# Revit family: ELP2_63_UN_Lightline_ETK
name_source: partatom
category: Lighting Fixtures
units: mm (PartAtom-declared; Revit-internal decimal feet)

## family parameters
Always vertical = No
Cut with Voids When Loaded = No
Light Source = Yes
OmniClass Number = 23.80.70.00
OmniClass Title = Lighting
Part Type = Normal
Room Calculation Point = Yes
Round Connector Dimension = Use Diameter
Shared = No
Work Plane-Based = No

## types (128) — shared parameters
Assembly Code = 63.0
Color Filter = 16777215
Description = Lightline
Dimming Lamp Color Temperature Shift = <None>
Emit Shape Visible in Rendering = No
Emit from Rectangle Length = 68 mm
Emit from Rectangle Width = 1482 mm  [stored 4.8622 ft]
IfcExportAs = IfcLightFixtureType
IfcExportType = USERDEFINED
Lamp = LED
Length = 1482 mm  [stored 4.8622 ft]
Luminaire_Body_Material = PPS Plastic
Manufacturer = ETK licht B.V.
Model = ELP2
Tilt Angle = 90.00°
URL = https://www.etk.nl
Voltage = 230 V

## per-type parameters (varying)
| type | Apparent Load | Photometric Web File | Wattage Comments |
| ELP.8673.15 | 118 VA | ELP.8673.15.ies | 118 W |
| ELP.8670.15 | 118 VA | ELP.8670.15.ies | 118 W |
| ELP.8663.15 | 118 VA | ELP.8663.15.ies | 118 W |
| ELP.8660.15 | 118 VA | ELP.8660.15.ies | 118 W |
| ELP.8653.15 | 80 VA | ELP.8653.15.ies | 80 W |
| ELP.8650.15 | 80 VA | ELP.8650.15.ies | 80 W |
| ELP.8643.15 | 80 VA | ELP.8643.15.ies | 80 W |
| ELP.8640.15 | 80 VA | ELP.8640.15.ies | 80 W |
| ELP.8633.15 | 61 VA | ELP.8633.15.ies | 61 W |
| ELP.8630.15 | 61 VA | ELP.8630.15.ies | 61 W |
| ELP.8623.15 | 61 VA | ELP.8623.15.ies | 61 W |
| ELP.8620.15 | 61 VA | ELP.8620.15.ies | 61 W |
| ELP.8613.15 | 43 VA | ELP.8613.15.ies | 43 W |
| ELP.8610.15 | 43 VA | ELP.8610.15.ies | 43 W |
| ELP.8603.15 | 43 VA | ELP.8603.15.ies | 43 W |
| ELP.8600.15 | 43 VA | ELP.8600.15.ies | 43 W |
| ELP.8573.15 | 118 VA | ELP.8573.15.ies | 118 W |
| ELP.8570.15 | 118 VA | ELP.8570.15.ies | 118 W |
| ELP.8563.15 | 118 VA | ELP.8563.15.ies | 118 W |
| ELP.8560.15 | 118 VA | ELP.8560.15.ies | 118 W |
| ELP.8553.15 | 80 VA | ELP.8553.15.ies | 80 W |
| ELP.8550.15 | 80 VA | ELP.8550.15.ies | 80 W |
| ELP.8543.15 | 80 VA | ELP.8543.15.ies | 80 W |
| ELP.8540.15 | 80 VA | ELP.8540.15.ies | 80 W |
| ELP.8533.15 | 61 VA | ELP.8533.15.ies | 61 W |
| ELP.8530.15 | 61 VA | ELP.8530.15.ies | 61 W |
| ELP.8523.15 | 61 VA | ELP.8523.15.ies | 61 W |
| ELP.8520.15 | 61 VA | ELP.8520.15.ies | 61 W |
| ELP.8513.15 | 43 VA | ELP.8513.15.ies | 43 W |
| ELP.8510.15 | 43 VA | ELP.8510.15.ies | 43 W |
| ELP.8503.15 | 43 VA | ELP.8503.15.ies | 43 W |
| ELP.8500.15 | 43 VA | ELP.8500.15.ies | 43 W |
| ELP.8473.15 | 118 VA | ELP.8473.15.ies | 118 W |
| ELP.8470.15 | 118 VA | ELP.8470.15.ies | 118 W |
| ELP.8463.15 | 118 VA | ELP.8463.15.ies | 118 W |
| ELP.8460.15 | 118 VA | ELP.8460.15.ies | 118 W |
| ELP.8453.15 | 80 VA | ELP.8453.15.ies | 80 W |
| ELP.8450.15 | 80 VA | ELP.8450.15.ies | 80 W |
| ELP.8443.15 | 80 VA | ELP.8443.15.ies | 80 W |
| ELP.8440.15 | 80 VA | ELP.8440.15.ies | 80 W |
| ELP.8433.15 | 61 VA | ELP.8433.15.ies | 61 W |
| ELP.8430.15 | 61 VA | ELP.8430.15.ies | 61 W |
| ELP.8423.15 | 61 VA | ELP.8423.15.ies | 61 W |
| ELP.8420.15 | 61 VA | ELP.8420.15.ies | 61 W |
| ELP.8413.15 | 43 VA | ELP.8413.15.ies | 43 W |
| ELP.8410.15 | 43 VA | ELP.8410.15.ies | 43 W |
| ELP.8403.15 | 43 VA | ELP.8403.15.ies | 43 W |
| ELP.8400.15 | 43 VA | ELP.8400.15.ies | 43 W |
| ELP.8393.15.HE | 114 VA | ELP.8393.15.HE.ies | 114 W |
| ELP.8390.15.HE | 114 VA | ELP.8390.15.HE.ies | 114 W |
| ELP.8383.15.HE | 114 VA | ELP.8383.15.HE.ies | 114 W |
| ELP.8380.15.HE | 114 VA | ELP.8380.15.HE.ies | 114 W |
| ELP.8373.15 | 118 VA | ELP.8373.15.ies | 118 W |
| ELP.8370.15 | 118 VA | ELP.8370.15.ies | 118 W |
| ELP.8363.15 | 118 VA | ELP.8363.15.ies | 118 W |
| ELP.8360.15 | 118 VA | ELP.8360.15.ies | 118 W |
| ELP.8353.15 | 80 VA | ELP.8353.15.ies | 80 W |
| ELP.8350.15 | 80 VA | ELP.8350.15.ies | 80 W |
| ELP.8343.15 | 80 VA | ELP.8343.15.ies | 80 W |
| ELP.8340.15 | 80 VA | ELP.8340.15.ies | 80 W |
| ELP.8333.15 | 61 VA | ELP.8333.15.ies | 61 W |
| ELP.8330.15 | 61 VA | ELP.8330.15.ies | 61 W |
| ELP.8323.15 | 61 VA | ELP.8323.15.ies | 61 W |
| ELP.8320.15 | 61 VA | ELP.8320.15.ies | 61 W |
| ELP.8313.15 | 43 VA | ELP.8313.15.ies | 43 W |
| ELP.8310.15 | 43 VA | ELP.8310.15.ies | 43 W |
| ELP.8303.15 | 43 VA | ELP.8303.15.ies | 43 W |
| ELP.8300.15 | 43 VA | ELP.8300.15.ies | 43 W |
| ELP.8293.15.HE | 114 VA | ELP.8293.15.HE.ies | 114 W |
| ELP.8290.15.HE | 114 VA | ELP.8290.15.HE.ies | 114 W |
| ELP.8283.15.HE | 114 VA | ELP.8283.15.HE.ies | 114 W |
| ELP.8280.15.HE | 114 VA | ELP.8280.15.HE.ies | 114 W |
| ELP.8273.15 | 118 VA | ELP.8273.15.ies | 118 W |
| ELP.8270.15 | 118 VA | ELP.8270.15.ies | 118 W |
| ELP.8263.15 | 118 VA | ELP.8263.15.ies | 118 W |
| ELP.8260.15 | 118 VA | ELP.8260.15.ies | 118 W |
| ELP.8253.15 | 80 VA | ELP.8253.15.ies | 80 W |
| ELP.8250.15 | 80 VA | ELP.8250.15.ies | 80 W |
| ELP.8243.15 | 80 VA | ELP.8243.15.ies | 80 W |
| ELP.8240.15 | 80 VA | ELP.8240.15.ies | 80 W |
| ELP.8233.15 | 61 VA | ELP.8233.15.ies | 61 W |
| ELP.8230.15 | 61 VA | ELP.8230.15.ies | 61 W |
| ELP.8223.15 | 61 VA | ELP.8223.15.ies | 61 W |
| ELP.8220.15 | 61 VA | ELP.8220.15.ies | 61 W |
| ELP.8213.15 | 43 VA | ELP.8213.15.ies | 43 W |
| ELP.8210.15 | 43 VA | ELP.8210.15.ies | 43 W |
| ELP.8203.15 | 43 VA | ELP.8203.15.ies | 43 W |
| ELP.8200.15 | 43 VA | ELP.8200.15.ies | 43 W |
| ELP.8193.15.HE | 114 VA | ELP.8193.15.HE.ies | 114 W |
| ELP.8190.15.HE | 114 VA | ELP.8190.15.HE.ies | 114 W |
| ELP.8183.15.HE | 114 VA | ELP.8183.15.HE.ies | 114 W |
| ELP.8180.15.HE | 114 VA | ELP.8180.15.HE.ies | 114 W |
| ELP.8173.15 | 118 VA | ELP.8173.15.ies | 118 W |
| ELP.8170.15 | 118 VA | ELP.8170.15.ies | 118 W |
| ELP.8163.15 | 118 VA | ELP.8163.15.ies | 118 W |
| ELP.8160.15 | 118 VA | ELP.8160.15.ies | 118 W |
| ELP.8153.15 | 80 VA | ELP.8153.15.ies | 80 W |
| ELP.8150.15 | 80 VA | ELP.8150.15.ies | 80 W |
| ELP.8143.15 | 80 VA | ELP.8143.15.ies | 80 W |
| ELP.8140.15 | 80 VA | ELP.8140.15.ies | 80 W |
| ELP.8133.15 | 61 VA | ELP.8133.15.ies | 61 W |
| ELP.8130.15 | 61 VA | ELP.8130.15.ies | 61 W |
| ELP.8123.15 | 61 VA | ELP.8123.15.ies | 61 W |
| ELP.8120.15 | 61 VA | ELP.8120.15.ies | 61 W |
| ELP.8113.15 | 43 VA | ELP.8113.15.ies | 43 W |
| ELP.8110.15 | 43 VA | ELP.8110.15.ies | 43 W |
| ELP.8103.15 | 43 VA | ELP.8103.15.ies | 43 W |
| ELP.8100.15 | 43 VA | ELP.8100.15.ies | 43 W |
| ELP.8093.15.HE | 114 VA | ELP.8093.15.HE.ies | 114 W |
| ELP.8090.15.HE | 114 VA | ELP.8090.15.HE.ies | 114 W |
| ELP.8083.15.HE | 114 VA | ELP.8083.15.HE.ies | 114 W |
| ELP.8080.15.HE | 114 VA | ELP.8080.15.HE.ies | 114 W |
| ELP.8073.15 | 118 VA | ELP.8073.15.ies | 118 W |
| ELP.8070.15 | 118 VA | ELP.8070.15.ies | 118 W |
| ELP.8063.15 | 118 VA | ELP.8063.15.ies | 118 W |
| ELP.8060.15 | 118 VA | ELP.8060.15.ies | 118 W |
| ELP.8053.15 | 80 VA | ELP.8053.15.ies | 80 W |
| ELP.8050.15 | 80 VA | ELP.8050.15.ies | 80 W |
| ELP.8043.15 | 80 VA | ELP.8043.15.ies | 80 W |
| ELP.8040.15 | 80 VA | ELP.8040.15.ies | 80 W |
| ELP.8033.15 | 61 VA | ELP.8033.15.ies | 61 W |
| ELP.8030.15 | 61 VA | ELP.8030.15.ies | 61 W |
| ELP.8023.15 | 61 VA | ELP.8023.15.ies | 61 W |
| ELP.8020.15 | 61 VA | ELP.8020.15.ies | 61 W |
| ELP.8013.15 | 43 VA | ELP.8013.15.ies | 43 W |
| ELP.8010.15 | 43 VA | ELP.8010.15.ies | 43 W |
| ELP.8003.15 | 43 VA | ELP.8003.15.ies | 43 W |
| ELP.8000.15 | 43 VA | ELP.8000.15.ies | 43 W |

note: [stored X ft] marks values corroborated as IEEE doubles in the binary element streams (Revit-internal decimal feet)

## geometry (parser evidence)
native form markers: Sweep x15
no freeform markers — native parametric forms only
